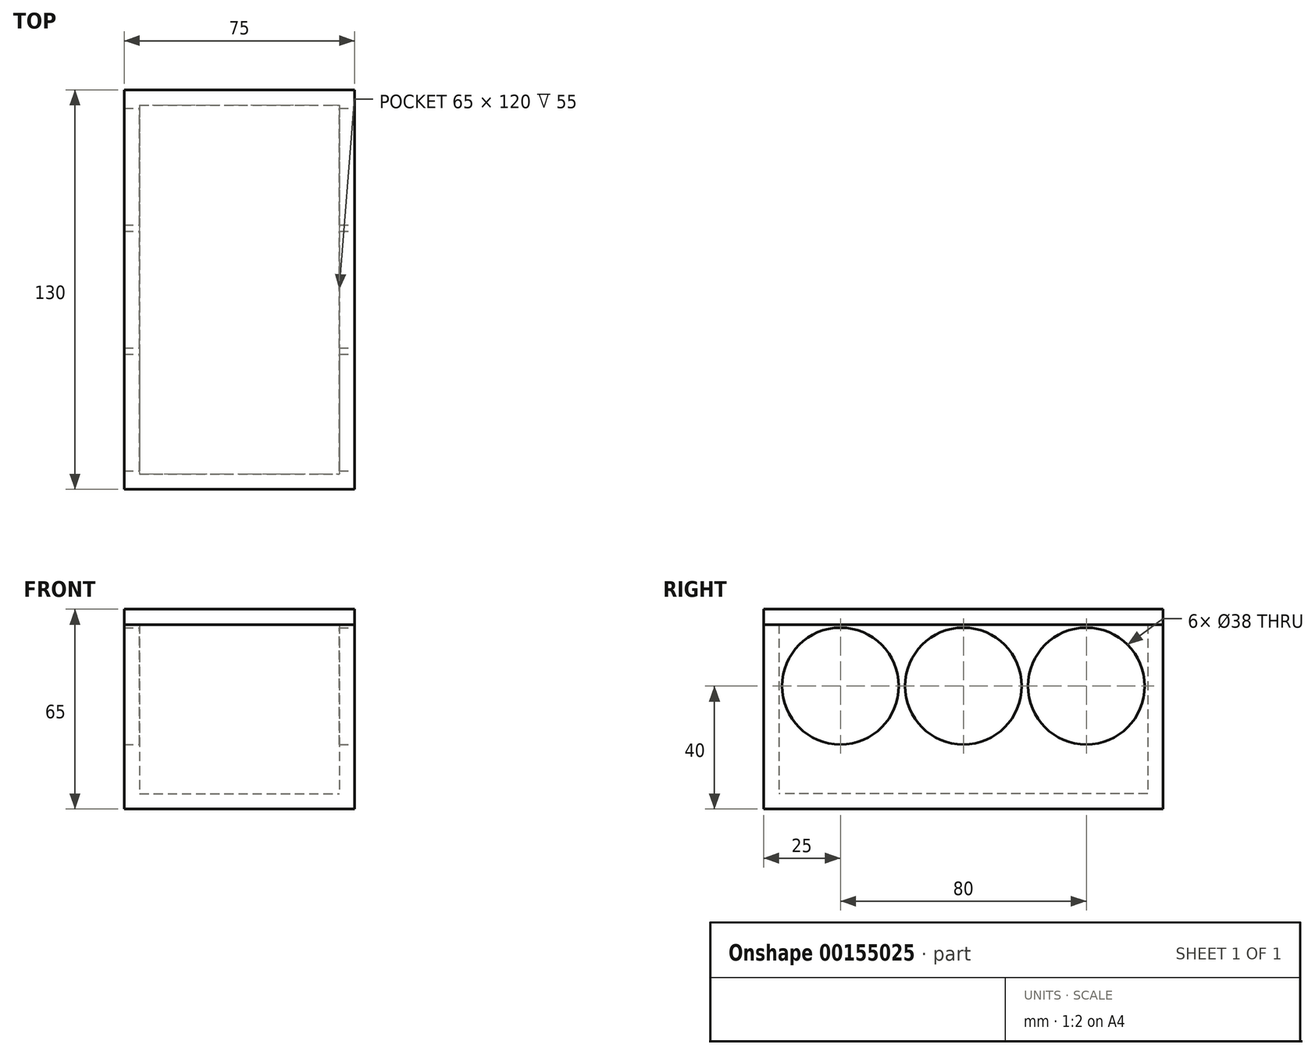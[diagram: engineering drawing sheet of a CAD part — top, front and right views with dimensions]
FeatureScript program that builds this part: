
annotation { "Feature Type Name" : "Feature", "Feature Type Description" : "" }
export const myFeature = defineFeature(function(context is Context, id is Id, definition is map)
    precondition{}
    {
        {
            var Q0;
            Q0=qCreatedBy(makeId("Top.planeOp"),FACE);
            var sketch = newSketch(context, id + "F0", { "sketchPlane" : qUnion([Q0])});
            skLineSegment(sketch, "E0.bottom", {"start": v(-37.5, 65) * mm, "end": v(37.5, 65) * mm});
            skLineSegment(sketch, "E0.top", {"start": v(-37.5, -65) * mm, "end": v(37.5, -65) * mm});
            skLineSegment(sketch, "E0.left", {"start": v(-37.5, 65) * mm, "end": v(-37.5, -65) * mm});
            skLineSegment(sketch, "E0.right", {"start": v(37.5, 65) * mm, "end": v(37.5, -65) * mm});
            skPoint(sketch, "E0.middle", {"position": v(0, 0) * mm});
            skLineSegment(sketch, "E1.0", {"start": v(32.5, 60) * mm, "end": v(32.5, -60) * mm});
            skLineSegment(sketch, "E1.1", {"start": v(-32.5, 60) * mm, "end": v(32.5, 60) * mm});
            skLineSegment(sketch, "E1.2", {"start": v(-32.5, 60) * mm, "end": v(-32.5, -60) * mm});
            skLineSegment(sketch, "E1.3", {"start": v(-32.5, -60) * mm, "end": v(32.5, -60) * mm});
            skSolve(sketch);
        }
        {
            var Q0;
            Q0=makeQuery(id+"F0.imprint","IMPRINT",FACE,{"disambiguationData":[TD([[makeQuery(id+"F0.imprint","IMPRINT",EDGE,{"derivedFrom":sQuery(id+"F0.wireOp",EDGE,"E0.bottom")}),-1.0]])]});
            extrude(context, id + "F1", {"entities" : qUnion([Q0]), "depth" : 55 * mm});
        }
        {
            var Q0;
            Q0=qCreatedBy(makeId("Top.planeOp"),FACE);
            var sketch = newSketch(context, id + "F2", { "sketchPlane" : qUnion([Q0])});
            skLineSegment(sketch, "E2.bottom", {"start": v(37.5, 65) * mm, "end": v(-37.5, 65) * mm});
            skLineSegment(sketch, "E2.top", {"start": v(37.5, -65) * mm, "end": v(-37.5, -65) * mm});
            skLineSegment(sketch, "E2.left", {"start": v(37.5, 65) * mm, "end": v(37.5, -65) * mm});
            skLineSegment(sketch, "E2.right", {"start": v(-37.5, 65) * mm, "end": v(-37.5, -65) * mm});
            skSolve(sketch);
        }
        {
            var Q0;
            Q0 = qSketchRegion(id + "F2", true);
            extrude(context, id + "F3", {"entities" : qUnion([Q0]), "operationType" : NewBodyOperationType.ADD, "oppositeDirection" : true, "depth" : 5 * mm});
        }
        {
            var Q0;
            Q0=makeQuery(id+"F1.opExtrude","CAP_FACE",FACE,{"disambiguationData":[OSD([sQuery(id+"F0.wireOp",EDGE,"E0.bottom"),sQuery(id+"F0.wireOp",EDGE,"E0.top"),sQuery(id+"F0.wireOp",EDGE,"E0.left"),sQuery(id+"F0.wireOp",EDGE,"E0.right"),sQuery(id+"F0.wireOp",EDGE,"E1.0"),sQuery(id+"F0.wireOp",EDGE,"E1.1"),sQuery(id+"F0.wireOp",EDGE,"E1.2"),sQuery(id+"F0.wireOp",EDGE,"E1.3")])],"isStart":false});
            var sketch = newSketch(context, id + "F4", { "sketchPlane" : qUnion([Q0])});
            skLineSegment(sketch, "E3.bottom", {"start": v(-37.5, -65) * mm, "end": v(37.5, -65) * mm});
            skLineSegment(sketch, "E3.top", {"start": v(-37.5, 65) * mm, "end": v(37.5, 65) * mm});
            skLineSegment(sketch, "E3.left", {"start": v(-37.5, -65) * mm, "end": v(-37.5, 65) * mm});
            skLineSegment(sketch, "E3.right", {"start": v(37.5, -65) * mm, "end": v(37.5, 65) * mm});
            skSolve(sketch);
        }
        {
            var Q0;
            Q0 = qSketchRegion(id + "F4", true);
            extrude(context, id + "F5", {"entities" : qUnion([Q0]), "depth" : 5 * mm});
        }
        {
            var Q0;
            Q0=makeQuery(id+"F3.boolean.opBoolean","MERGE",FACE,{"derivedFrom":[makeQuery(id+"F1.opExtrude","SWEPT_FACE",FACE,{"disambiguationData":[OSD([sQuery(id+"F0.wireOp",EDGE,"E0.right")])]}),makeQuery(id+"F3.opExtrude","SWEPT_FACE",FACE,{"disambiguationData":[OSD([sQuery(id+"F2.wireOp",EDGE,"E2.left")])]})]});
            var sketch = newSketch(context, id + "F6", { "sketchPlane" : qUnion([Q0])});
            skCircle(sketch, "E4", {"center": v(-40, 35) * mm, "radius": 19 * mm});
            skCircle(sketch, "E5", {"center": v(0, 35) * mm, "radius": 19 * mm});
            skCircle(sketch, "E6", {"center": v(40, 35) * mm, "radius": 19 * mm});
            skLineSegment(sketch, "E7", {"start": v(-40, 35) * mm, "end": v(0, 35) * mm, "construction": true});
            skLineSegment(sketch, "E8", {"start": v(0, 35) * mm, "end": v(40, 35) * mm, "construction": true});
            skSolve(sketch);
        }
        {
            var Q0;
            Q0 = qSketchRegion(id + "F6", true);
            extrude(context, id + "F7", {"entities" : qUnion([Q0]), "operationType" : NewBodyOperationType.REMOVE, "endBound" : BoundingType.THROUGH_ALL, "oppositeDirection" : true, "depth" : 25 * mm});
        }
    });
